# Revit family: Table-Teknion-NFTT_Wood_Table_Rectangular-R2020
name_source: partatom
category: Furniture
units: mm (PartAtom-declared; Revit-internal decimal feet)

## family parameters
Always vertical = Yes
Cut with Voids When Loaded = No
OmniClass Number = 23.40.20.00
OmniClass Title = General Furniture and Specialties
Room Calculation Point = No
Shared = Yes
Work Plane-Based = No

## types (2) — shared parameters
Assembly Code = E2020200
Electrical Finish = Paint-Teknion-23-Z-Foundation-Foundry Onyx
Foot Finish = Paint - Teknion - 52 - Ebony
Manufacturer = Teknion
Manufacturer Fax = 416.661.4586
Part Number = NFTT
Product Line = North 56
Product Page URL = https://www.teknion.com
Series = North 56
Sustainability Data = https://www.teknion.com
URL = www.teknion.com
Unit Weight URL = http://www.teknion.com
Warranty = http://www.teknion.com
zero-valued in all types: Default Elevation

## per-type parameters (varying)
| type | Bracket Finish | Description | Frame Finish | Hardware Finish | Leg Wood Finish | Model | Worksurface Finish |
| Split Two Piece Top | Seamless Paint - Teknion - 25 - Crisp Grey | Wood Table - Rectangular, Split Two Piece Top, 29" Height, 40" Depth | Veneer - Teknion - WX - Empress Walnut | Seamless Paint - Teknion - 25 - Crisp Grey | Veneer - Teknion - WX - Empress Walnut | NFTTT2940_ | Veneer - Teknion - MP - Natural Maple |
| Standard Top | Paint-Teknion-23-Z-Foundation-Foundry Onyx | Wood Table - Standard Top, 29" Height, 40" Depth | Veneer -Teknion - UU - Rustic Oak - Sierra | Paint-Teknion-23-Z-Foundation-Foundry Onyx | Veneer -Teknion - UU - Rustic Oak - Sierra | NFTTS2940_ | Veneer -Teknion - UU - Rustic Oak - Sierra |

type visibility flags: 2 boolean params named "<type name>" — each type sets only its own to Yes (folded from table)

## geometry (parser evidence)
native form markers: Sweep x7
no freeform markers — native parametric forms only
